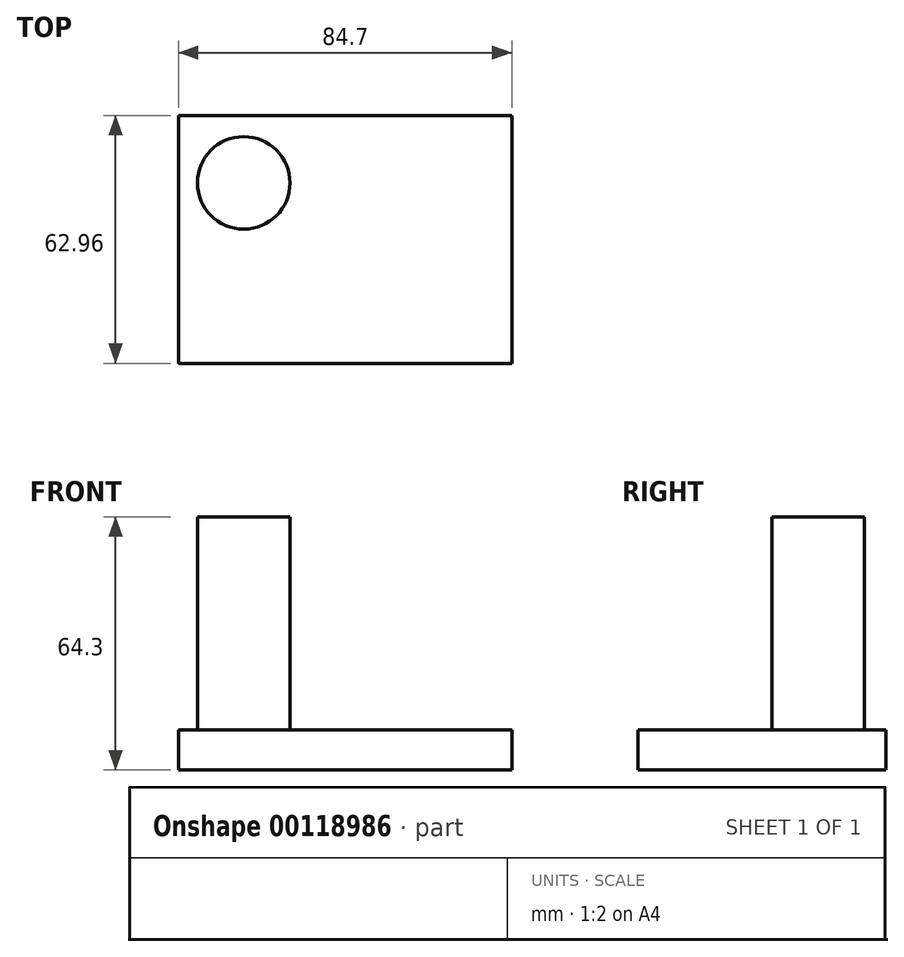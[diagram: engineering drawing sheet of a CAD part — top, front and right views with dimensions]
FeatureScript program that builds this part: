
annotation { "Feature Type Name" : "Feature", "Feature Type Description" : "" }
export const myFeature = defineFeature(function(context is Context, id is Id, definition is map)
    precondition{}
    {
        {
            var Q0;
            Q0=qCreatedBy(makeId("Top.planeOp"),FACE);
            var sketch = newSketch(context, id + "F0", { "sketchPlane" : qUnion([Q0])});
            skLineSegment(sketch, "E0.bottom", {"start": v(-36.85, -27.14) * mm, "end": v(47.85, -27.14) * mm});
            skLineSegment(sketch, "E0.top", {"start": v(-36.85, 35.82) * mm, "end": v(47.85, 35.82) * mm});
            skLineSegment(sketch, "E0.left", {"start": v(-36.85, -27.14) * mm, "end": v(-36.85, 35.82) * mm});
            skLineSegment(sketch, "E0.right", {"start": v(47.85, -27.14) * mm, "end": v(47.85, 35.82) * mm});
            skSolve(sketch);
        }
        {
            var Q0;
            Q0=makeQuery(id+"F0.imprint","IMPRINT",FACE,{"disambiguationData":[TD([[makeQuery(id+"F0.imprint","IMPRINT",EDGE,{"derivedFrom":sQuery(id+"F0.wireOp",EDGE,"E0.bottom")}),1.0]])]});
            extrude(context, id + "F1", {"entities" : qUnion([Q0]), "depth" : 10.16 * mm});
        }
        {
            var Q0;
            Q0=makeQuery(id+"F1.opExtrude","CAP_FACE",FACE,{"disambiguationData":[OSD([sQuery(id+"F0.wireOp",EDGE,"E0.bottom"),sQuery(id+"F0.wireOp",EDGE,"E0.top"),sQuery(id+"F0.wireOp",EDGE,"E0.left"),sQuery(id+"F0.wireOp",EDGE,"E0.right")])],"isStart":false});
            var sketch = newSketch(context, id + "F2", { "sketchPlane" : qUnion([Q0])});
            skSolve(sketch);
        }
        {
            var Q0;
            Q0=makeQuery(id+"F2.imprint","IMPRINT",FACE,{"disambiguationData":[TD([[makeQuery(id+"F2.imprint","IMPRINT",EDGE,{"derivedFrom":makeQuery(id+"F1.opExtrude","CAP_EDGE",EDGE,{"disambiguationData":[OSD([sQuery(id+"F0.wireOp",EDGE,"E0.bottom")])],"isStart":false})}),1.0]])]});
            var sketch = newSketch(context, id + "F3", { "sketchPlane" : qUnion([Q0])});
            skCircle(sketch, "E1", {"center": v(-20.3, 18.7) * mm, "radius": 11.76 * mm});
            skSolve(sketch);
        }
        {
            var Q0;
            Q0=makeQuery(id+"F3.imprint","IMPRINT",FACE,{"disambiguationData":[TD([[makeQuery(id+"F3.imprint","IMPRINT",EDGE,{"derivedFrom":sQuery(id+"F3.wireOp",EDGE,"E1")}),1.0]])]});
            extrude(context, id + "F4", {"entities" : qUnion([Q0]), "operationType" : NewBodyOperationType.ADD, "depth" : 54.14 * mm});
        }
    });
